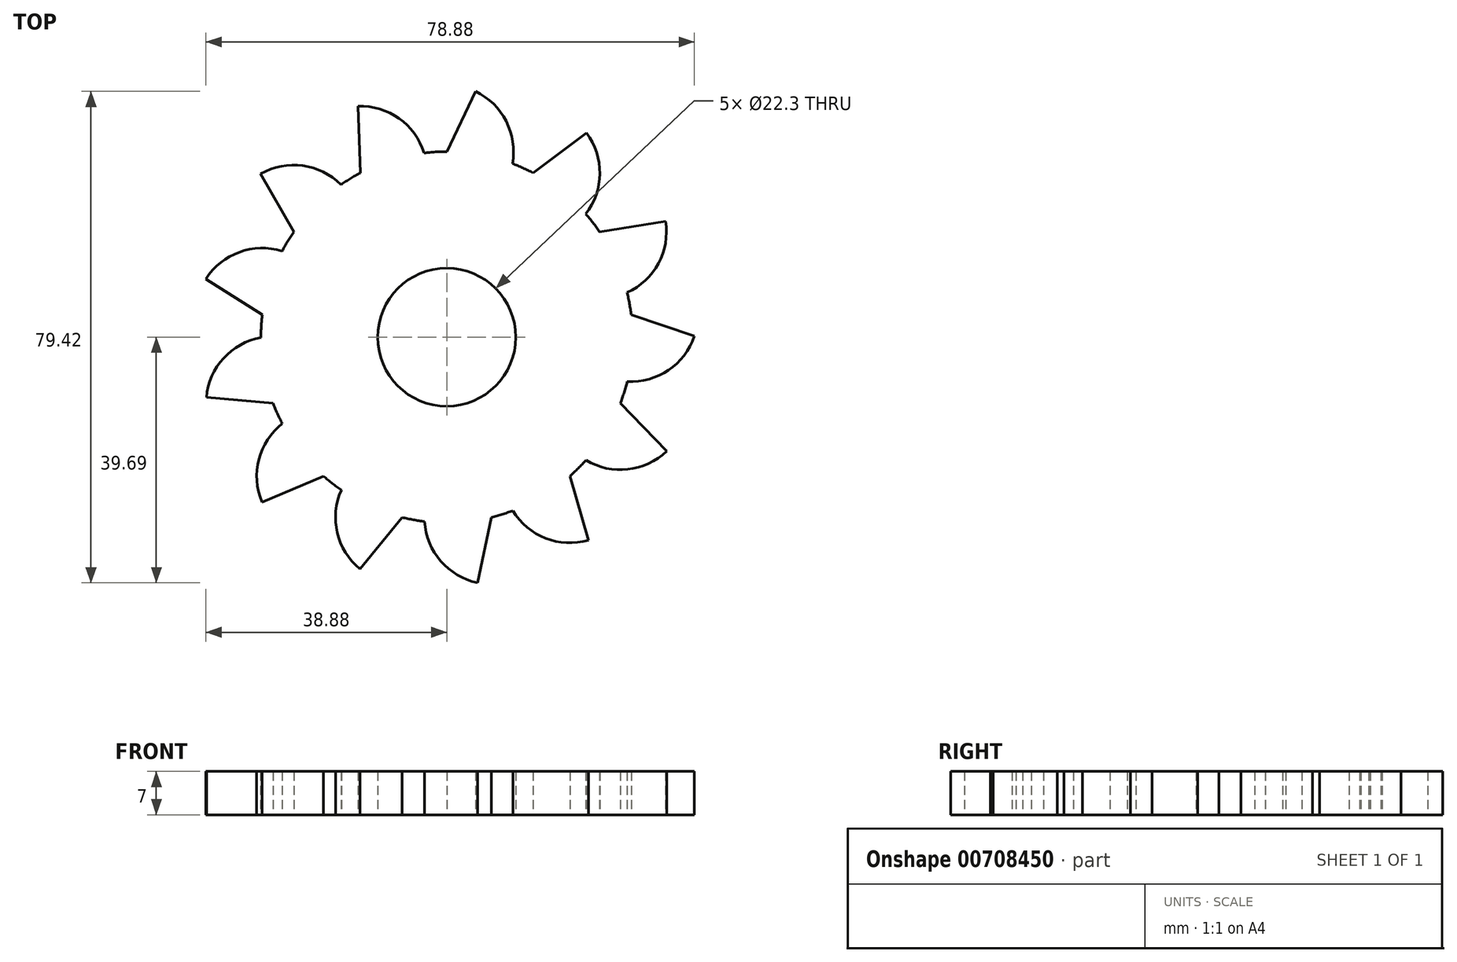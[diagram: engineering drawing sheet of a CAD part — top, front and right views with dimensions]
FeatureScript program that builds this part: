
annotation { "Feature Type Name" : "Feature", "Feature Type Description" : "" }
export const myFeature = defineFeature(function(context is Context, id is Id, definition is map)
    precondition{}
    {
        {
            var Q0;
            Q0=qCreatedBy(makeId("Top.planeOp"),FACE);
            var sketch = newSketch(context, id + "F0", { "sketchPlane" : qUnion([Q0])});
            skCircle(sketch, "E0", {"center": v(0, 0) * mm, "radius": 11.15 * mm});
            skCircle(sketch, "E1", {"center": v(0, 0) * mm, "radius": 30 * mm});
            skCircle(sketch, "E2", {"center": v(0, 0) * mm, "radius": 40 * mm, "construction": true});
            skArc(sketch, "E3", {"start": v(4.65, 39.73) * mm, "mid": v(9.6, 34.9) * mm, "end": v(10.6, 28.06) * mm});
            skLineSegment(sketch, "E4", {"start": v(4.65, 39.73) * mm, "end": v(0, 30) * mm});
            skLineSegment(sketch, "E5.1.0", {"start": v(-14.34, 37.34) * mm, "end": v(-13.94, 26.56) * mm});
            skArc(sketch, "E5.1.1", {"start": v(-14.34, 37.34) * mm, "mid": v(-7.72, 35.37) * mm, "end": v(-3.65, 29.78) * mm});
            skLineSegment(sketch, "E5.2.0", {"start": v(-30.05, 26.4) * mm, "end": v(-24.69, 17.04) * mm});
            skArc(sketch, "E5.2.1", {"start": v(-30.05, 26.4) * mm, "mid": v(-23.27, 27.73) * mm, "end": v(-17.07, 24.67) * mm});
            skLineSegment(sketch, "E6.2.3.0", {"start": v(-38.88, 9.4) * mm, "end": v(-29.78, 3.62) * mm});
            skArc(sketch, "E6.3.3.0", {"start": v(-38.88, 9.4) * mm, "mid": v(-33.5, 13.74) * mm, "end": v(-26.58, 13.91) * mm});
            skLineSegment(sketch, "E6.2.4.0", {"start": v(-38.8, -9.74) * mm, "end": v(-28.05, -10.64) * mm});
            skArc(sketch, "E6.3.4.0", {"start": v(-38.8, -9.74) * mm, "mid": v(-36.04, -3.4) * mm, "end": v(-30, -0.03) * mm});
            skLineSegment(sketch, "E6.2.5.0", {"start": v(-29.83, -26.65) * mm, "end": v(-19.9, -22.46) * mm});
            skArc(sketch, "E6.3.5.0", {"start": v(-29.83, -26.65) * mm, "mid": v(-30.33, -19.76) * mm, "end": v(-26.55, -13.97) * mm});
            skLineSegment(sketch, "E6.2.6.0", {"start": v(-14.02, -37.46) * mm, "end": v(-7.18, -29.13) * mm});
            skArc(sketch, "E6.3.6.0", {"start": v(-14.02, -37.46) * mm, "mid": v(-17.68, -31.6) * mm, "end": v(-17.02, -24.7) * mm});
            skLineSegment(sketch, "E6.2.7.0", {"start": v(5, -39.69) * mm, "end": v(7.18, -29.13) * mm});
            skArc(sketch, "E6.3.7.0", {"start": v(5, -39.69) * mm, "mid": v(-0.97, -36.19) * mm, "end": v(-3.58, -29.79) * mm});
            skLineSegment(sketch, "E6.2.8.0", {"start": v(22.86, -32.82) * mm, "end": v(19.9, -22.46) * mm});
            skArc(sketch, "E6.3.8.0", {"start": v(22.86, -32.82) * mm, "mid": v(15.96, -32.5) * mm, "end": v(10.67, -28.04) * mm});
            skLineSegment(sketch, "E6.2.9.0", {"start": v(35.5, -18.44) * mm, "end": v(28.05, -10.64) * mm});
            skArc(sketch, "E6.3.9.0", {"start": v(35.5, -18.44) * mm, "mid": v(29.23, -21.36) * mm, "end": v(22.48, -19.87) * mm});
            skLineSegment(sketch, "E7.2.10.0", {"start": v(40, 0.17) * mm, "end": v(29.78, 3.62) * mm});
            skArc(sketch, "E7.3.10.0", {"start": v(40, 0.17) * mm, "mid": v(35.8, -5.33) * mm, "end": v(29.14, -7.15) * mm});
            skLineSegment(sketch, "E7.2.11.0", {"start": v(35.34, 18.74) * mm, "end": v(24.69, 17.04) * mm});
            skArc(sketch, "E7.3.11.0", {"start": v(35.34, 18.74) * mm, "mid": v(34.18, 11.92) * mm, "end": v(29.12, 7.21) * mm});
            skLineSegment(sketch, "E8.2.12.0", {"start": v(22.58, 33.02) * mm, "end": v(13.94, 26.56) * mm});
            skArc(sketch, "E8.3.12.0", {"start": v(22.58, 33.02) * mm, "mid": v(24.72, 26.44) * mm, "end": v(22.43, 19.92) * mm});
            skSolve(sketch);
        }
        {
            var Q0;
            Q0 = qSketchRegion(id + "F0", true);
            extrude(context, id + "F1", {"entities" : qUnion([Q0]), "depth" : 7 * mm, "offsetDistance" : 25 * mm});
        }
    });
